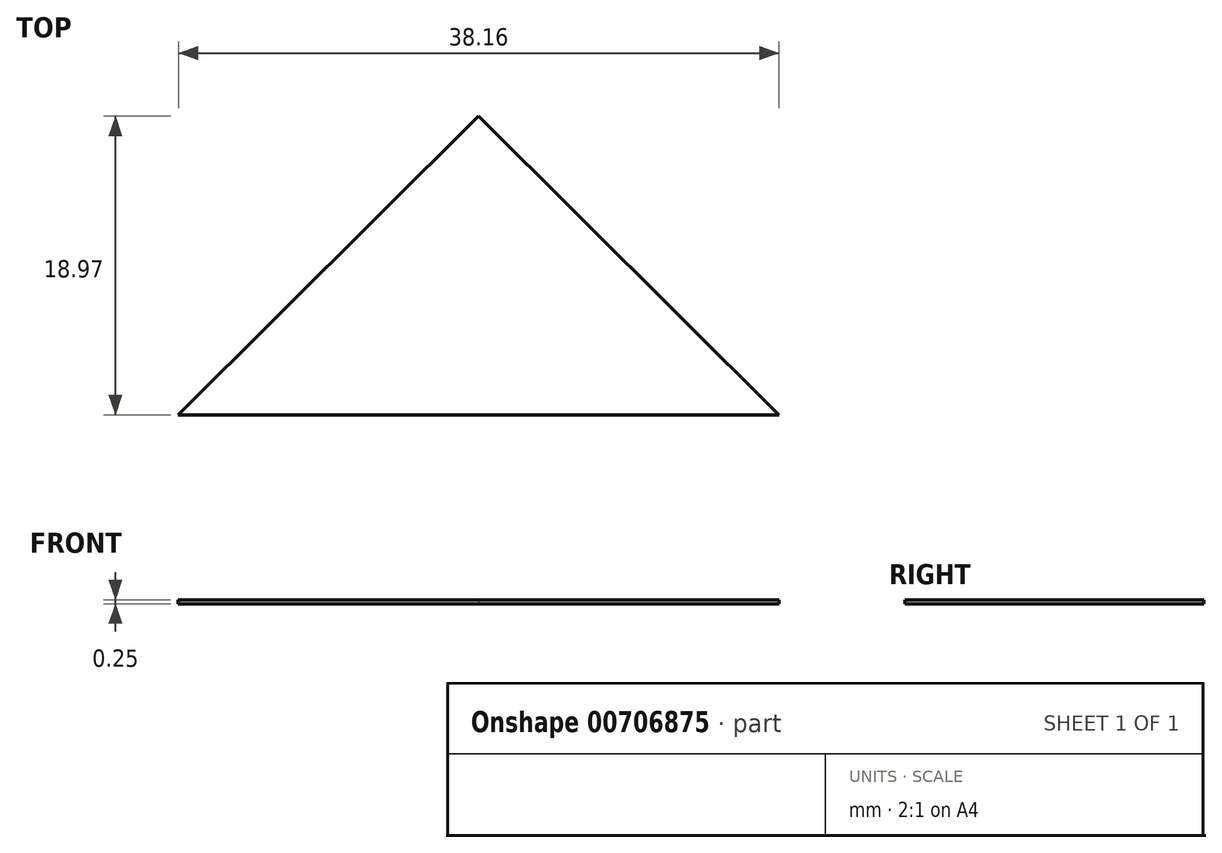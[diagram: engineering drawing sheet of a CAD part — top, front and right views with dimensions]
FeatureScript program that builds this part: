
annotation { "Feature Type Name" : "Feature", "Feature Type Description" : "" }
export const myFeature = defineFeature(function(context is Context, id is Id, definition is map)
    precondition{}
    {
        {
            var Q0;
            Q0=qCreatedBy(makeId("Top.planeOp"),FACE);
            var sketch = newSketch(context, id + "F0", { "sketchPlane" : qUnion([Q0])});
            skLineSegment(sketch, "E0", {"start": v(-44.43, -47.16) * mm, "end": v(-63.51, -28.2) * mm});
            skLineSegment(sketch, "E1", {"start": v(-63.51, -28.2) * mm, "end": v(-82.6, -47.16) * mm});
            skLineSegment(sketch, "E2", {"start": v(-82.6, -47.16) * mm, "end": v(-44.43, -47.16) * mm});
            skSolve(sketch);
        }
        {
            var Q0;
            Q0 = qSketchRegion(id + "F0", true);
            extrude(context, id + "F1", {"entities" : qUnion([Q0]), "depth" : 0.25 * mm, "offsetDistance" : 25.4 * mm});
        }
    });
